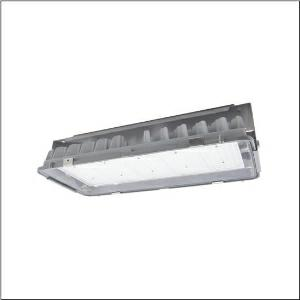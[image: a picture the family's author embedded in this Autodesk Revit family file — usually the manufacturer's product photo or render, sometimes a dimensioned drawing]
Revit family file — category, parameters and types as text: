
# Revit family: highbay_11xtreme_51hf61da4mma
name_source: partatom
category: Lighting Fixtures
units: mm (PartAtom-declared; Revit-internal decimal feet)

## family parameters
Cut with Voids When Loaded = No
Host = Face
Light Source = No
Part Type = Normal
Room Calculation Point = No
Round Connector Dimension = Use Diameter
Shared = No

## types (1)
- --- (1 x LED, 31500 lm, 170.8 W, 4000K)
    Apparent Load = 171 VA
    CIE Flux Codes = 88 96 99 100 100
    Color Rendering = 80
    Color Temperature = 4000K
    Default Elevation = 1800 mm
    Description = Highbay 11Xtreme, high bay luminaire, primary light control with lens, of PMMA, primary optical cover: cover, of toughened safety glass, light emission: direct distribution, primary light characteristic: symmetric, installation type: suspended mounting, surface-mounted, 1x LED module,for 1x LED, rated luminous flux: 31.500lm, luminous efficacy: 184lm/W, light colour: 840, colour temperature: 4000K, control gear: DALI 2, with cable H07RN-F 5x 1.5mm², mains connection: 220..240V, AC, 50/60Hz, cable length: 1,5m, rated input power: 171W, luminaire housing, of diecast aluminium, coated, silver, length: 595mm, width: 280mm, height: 195mm, protection rating (complete): IP66, insulation class (complete): insulation class I (protective earthing), certification: CE, ENEC, UKCA, protection symbol: D, ball protection: ball impact resistant according to DIN VDE 0710 part 13 (with chain suspension), impact resistance: IK08, permissible operating ambient temperature: -25..+60°C, reducing of maximum allowable ambient temperature of 5°C with ceiling mounting, packaging unit: 1 piece
    Height = 157 mm
    Lamp = 1 x LED
    Lamp Light Flux = 31500 lm
    Lamp Power = 170.8 W
    Lamp count = 1
    Length = 593 mm
    Luminous efficacy = 184 lm/W
    Manufacturer = Siteco
    ModVariant = No
    Model = 51HF61DA4MMA
    Mounting Place = Ceiling
    Mounting Type = Pendant
    Number of Poles = 1
    OnlyDefault = Yes
    Power Factor = 1
    Product Name = Highbay 11Xtreme
    Product group = high bay luminaire
    ProductGroupID = 902
    Protection Class = Protection class I
    Protection Degree = IP 66
    RLX_Detail_Level = 1
    RLX_Emergency_Light_Flux = 0 lm
    RLX_Emergency_Type = 0
    RLX_Emergency_Type_DB = No
    RlxData = <blob elided: 27905 chars, md5=40acf828>
    Socket = socket
    Standby Power = 0 W
    System Light Flux = 31501 lm
    System Power = 171 W
    Type Comments = factory setting: luminous flux: 100 % | dim-lin: 254 | 1132 mA
    Type Image = l_1258342.jpg
    URL = http://relux.com
    VarID = @adj_088491
    Voltage = 0 V
    Weight = 0.00 kg
    Width = 278 mm

## geometry (parser evidence)
native form markers: Blend x4, Sweep x12
no freeform markers — native parametric forms only
